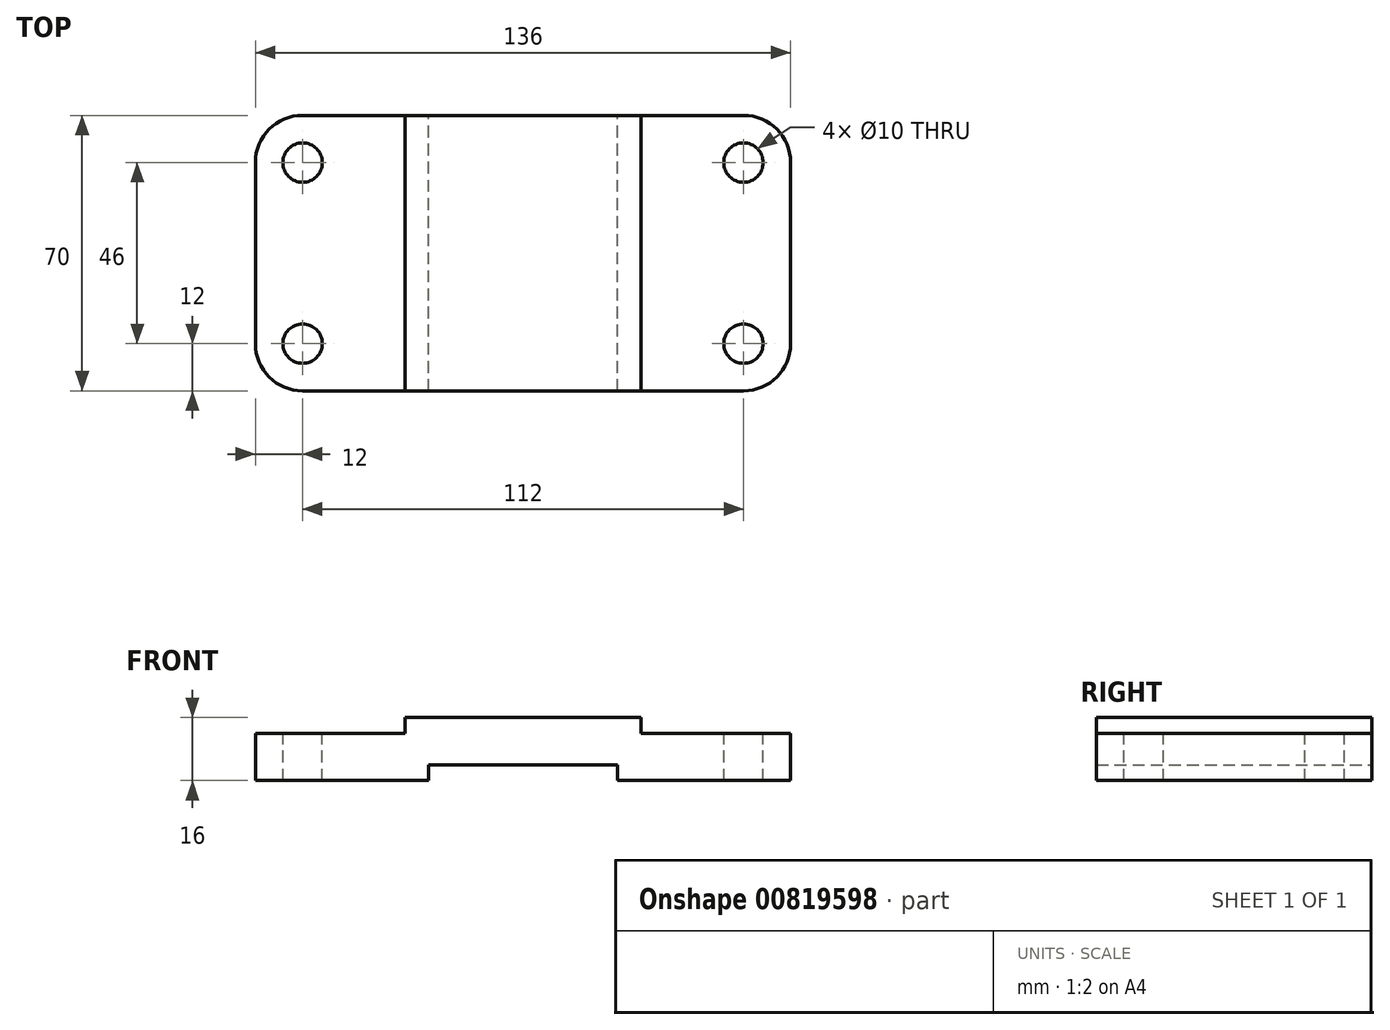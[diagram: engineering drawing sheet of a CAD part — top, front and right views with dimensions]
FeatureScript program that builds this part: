
annotation { "Feature Type Name" : "Feature", "Feature Type Description" : "" }
export const myFeature = defineFeature(function(context is Context, id is Id, definition is map)
    precondition{}
    {
        {
            var Q0;
            Q0=qCreatedBy(makeId("Front.planeOp"),FACE);
            var sketch = newSketch(context, id + "F0", { "sketchPlane" : qUnion([Q0])});
            skLineSegment(sketch, "E0.bottom", {"start": v(0, 0) * mm, "end": v(38, 0) * mm});
            skLineSegment(sketch, "E0.top", {"start": v(0, -12) * mm, "end": v(44, -12) * mm});
            skLineSegment(sketch, "E0.left", {"start": v(0, 0) * mm, "end": v(0, -12) * mm});
            skLineSegment(sketch, "E0.right", {"start": v(136, 0) * mm, "end": v(136, -12) * mm});
            skLineSegment(sketch, "E1", {"start": v(68, 4) * mm, "end": v(98, 4) * mm});
            skLineSegment(sketch, "E2", {"start": v(68, 4) * mm, "end": v(38, 4) * mm});
            skLineSegment(sketch, "E3", {"start": v(38, 4) * mm, "end": v(38, 0) * mm});
            skLineSegment(sketch, "E4", {"start": v(98, 4) * mm, "end": v(98, 0) * mm});
            skLineSegment(sketch, "E5.trimOffspring", {"start": v(98, 0) * mm, "end": v(136, 0) * mm});
            skLineSegment(sketch, "E6", {"start": v(44, -8) * mm, "end": v(92, -8) * mm});
            skPoint(sketch, "E7", {"position": v(68, -12) * mm});
            skPoint(sketch, "E8", {"position": v(68, -8) * mm});
            skLineSegment(sketch, "E9", {"start": v(44, -8) * mm, "end": v(44, -12) * mm});
            skLineSegment(sketch, "E10", {"start": v(92, -8) * mm, "end": v(92, -12) * mm});
            skLineSegment(sketch, "E11.trimOffspring", {"start": v(92, -12) * mm, "end": v(136, -12) * mm});
            skSolve(sketch);
        }
        {
            var Q0;
            Q0=makeQuery(id+"F0.imprint","IMPRINT",FACE,{"disambiguationData":[TD([[makeQuery(id+"F0.imprint","IMPRINT",EDGE,{"derivedFrom":sQuery(id+"F0.wireOp",EDGE,"E0.bottom")}),-1.0]])]});
            extrude(context, id + "F1", {"entities" : qUnion([Q0]), "endBound" : BoundingType.SYMMETRIC, "depth" : 70 * mm, "offsetDistance" : 25.4 * mm});
        }
        {
            var Q0;
            Q0=makeQuery(id+"F1.opExtrude","CAP_EDGE",EDGE,{"disambiguationData":[OSD([sQuery(id+"F0.wireOp",EDGE,"E0.left")])],"isStart":false});
            var Q1;
            Q1=makeQuery(id+"F1.opExtrude","CAP_EDGE",EDGE,{"disambiguationData":[OSD([sQuery(id+"F0.wireOp",EDGE,"E0.right")])],"isStart":false});
            var Q2;
            Q2=makeQuery(id+"F1.opExtrude","CAP_EDGE",EDGE,{"disambiguationData":[OSD([sQuery(id+"F0.wireOp",EDGE,"E0.right")])],"isStart":true});
            var Q3;
            Q3=makeQuery(id+"F1.opExtrude","CAP_EDGE",EDGE,{"disambiguationData":[OSD([sQuery(id+"F0.wireOp",EDGE,"E0.left")])],"isStart":true});
            fillet(context, id + "F2", {"entities" : qUnion([Q0, Q1, Q2, Q3]), "radius" : 12 * mm, "tangentPropagation" : true, "allowEdgeOverflow" : false});
        }
        {
            var Q0;
            Q0=makeQuery(id+"F1.opExtrude","SWEPT_FACE",FACE,{"disambiguationData":[OSD([sQuery(id+"F0.wireOp",EDGE,"E0.bottom")])]});
            var sketch = newSketch(context, id + "F3", { "sketchPlane" : qUnion([Q0])});
            skCircle(sketch, "E12", {"center": v(12, -23) * mm, "radius": 5 * mm});
            skCircle(sketch, "E13", {"center": v(12, 23) * mm, "radius": 5 * mm});
            skSolve(sketch);
        }
        {
            var Q0;
            Q0=makeQuery(id+"F3.imprint","IMPRINT",FACE,{"disambiguationData":[TD([[makeQuery(id+"F3.imprint","IMPRINT",EDGE,{"derivedFrom":sQuery(id+"F3.wireOp",EDGE,"E13")}),1.0]])]});
            var Q1;
            Q1=makeQuery(id+"F3.imprint","IMPRINT",FACE,{"disambiguationData":[TD([[makeQuery(id+"F3.imprint","IMPRINT",EDGE,{"derivedFrom":sQuery(id+"F3.wireOp",EDGE,"E12")}),1.0]])]});
            extrude(context, id + "F4", {"entities" : qUnion([Q0, Q1]), "operationType" : NewBodyOperationType.REMOVE, "oppositeDirection" : true, "depth" : 25.4 * mm, "offsetDistance" : 25.4 * mm});
        }
        {
            var Q0;
            Q0=makeQuery(id+"F1.opExtrude","SWEPT_FACE",FACE,{"disambiguationData":[OSD([sQuery(id+"F0.wireOp",EDGE,"E5.trimOffspring")])]});
            var sketch = newSketch(context, id + "F5", { "sketchPlane" : qUnion([Q0])});
            skCircle(sketch, "E14", {"center": v(124, 23) * mm, "radius": 5 * mm});
            skCircle(sketch, "E15", {"center": v(124, -23) * mm, "radius": 5 * mm});
            skSolve(sketch);
        }
        {
            var Q0;
            Q0=sQuery(id+"F5.wireOp",VERTEX,"E14.center");
            var Q1;
            Q1=sQuery(id+"F5.wireOp",VERTEX,"E15.center");
            var Q2;
            Q2=makeQuery(id+"F1.opExtrude","SWEPT_BODY",BODY,{"disambiguationData":[OSD([sQuery(id+"F0.wireOp",EDGE,"E0.bottom"),sQuery(id+"F0.wireOp",EDGE,"E0.top"),sQuery(id+"F0.wireOp",EDGE,"E0.left"),sQuery(id+"F0.wireOp",EDGE,"E0.right"),sQuery(id+"F0.wireOp",EDGE,"E1"),sQuery(id+"F0.wireOp",EDGE,"E2"),sQuery(id+"F0.wireOp",EDGE,"E3"),sQuery(id+"F0.wireOp",EDGE,"E4"),sQuery(id+"F0.wireOp",EDGE,"E5.trimOffspring"),sQuery(id+"F0.wireOp",EDGE,"E6"),sQuery(id+"F0.wireOp",EDGE,"E9"),sQuery(id+"F0.wireOp",EDGE,"E10"),sQuery(id+"F0.wireOp",EDGE,"E11.trimOffspring")])]});
            hole(context, id + "F6", {"style" : HoleStyle.SIMPLE, "endStyle" : HoleEndStyle.THROUGH, "holeDiameter" : 10 * mm, "majorDiameter" : 6.35 * mm, "isTappedThrough" : true, "tappedDepth" : 12.7 * mm, "tapClearance" : 3, "locations" : qUnion([Q0, Q1]), "scope" : qUnion([Q2])});
        }
    });
